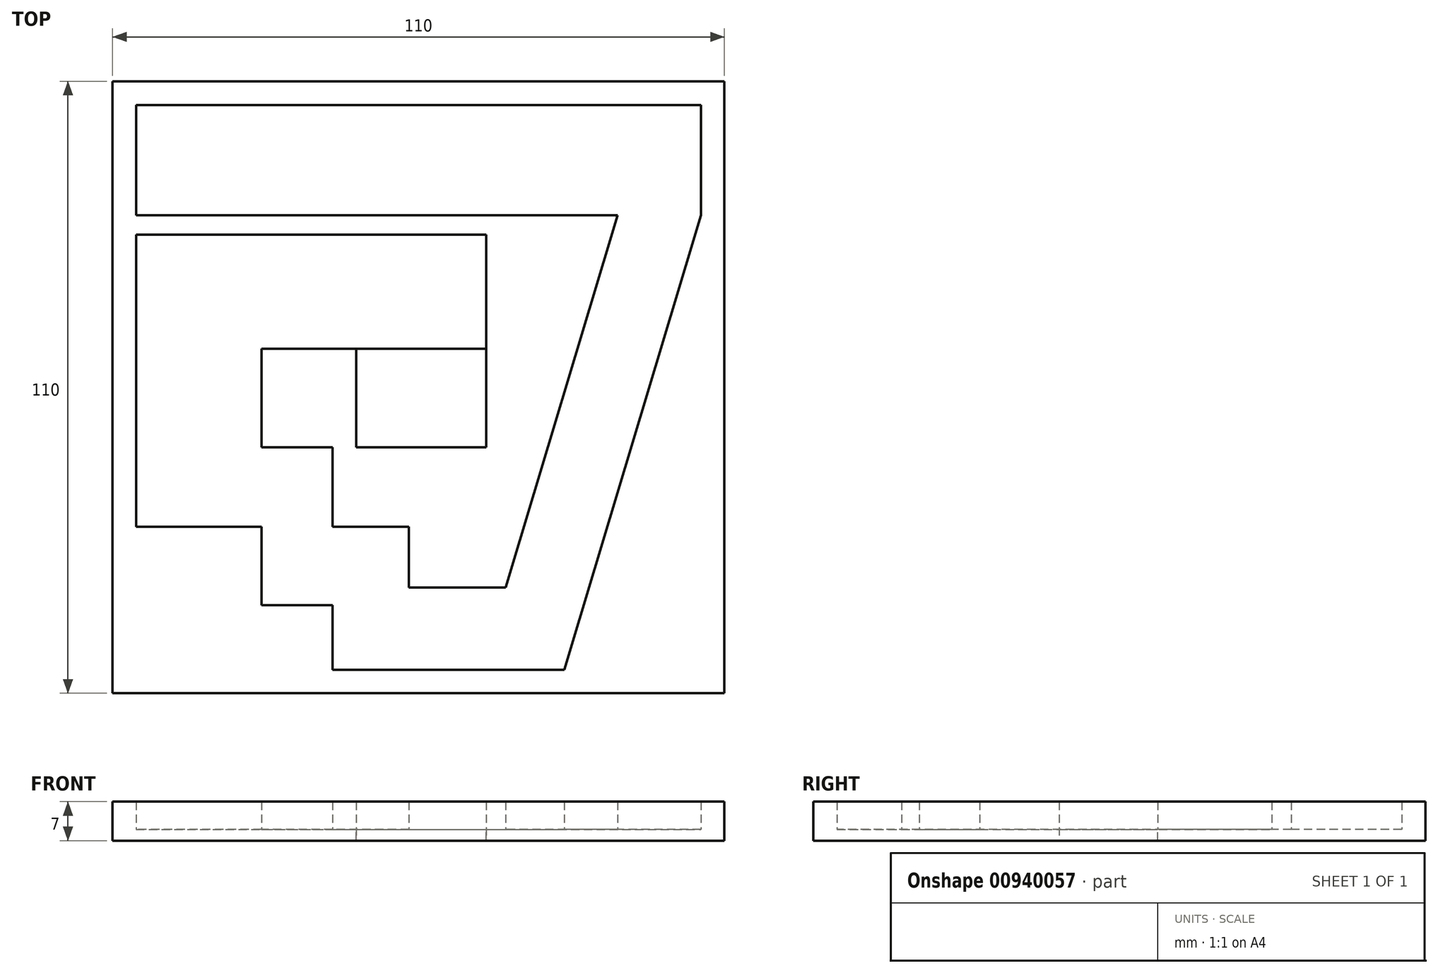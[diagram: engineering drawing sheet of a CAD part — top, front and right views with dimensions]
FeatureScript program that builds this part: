
annotation { "Feature Type Name" : "Feature", "Feature Type Description" : "" }
export const myFeature = defineFeature(function(context is Context, id is Id, definition is map)
    precondition{}
    {
        {
            var Q0;
            Q0=qCreatedBy(makeId("Top.planeOp"),FACE);
            var sketch = newSketch(context, id + "F0", { "sketchPlane" : qUnion([Q0])});
            skLineSegment(sketch, "E0.bottom", {"start": v(-49.05, 49.29) * mm, "end": v(52.5, 49.29) * mm});
            skLineSegment(sketch, "E0.top", {"start": v(-53.28, -56.48) * mm, "end": v(-13.73, -56.48) * mm});
            skLineSegment(sketch, "E0.right", {"start": v(52.5, 49.29) * mm, "end": v(52.5, 29.44) * mm});
            skLineSegment(sketch, "E1", {"start": v(-49.05, 29.44) * mm, "end": v(37.49, 29.44) * mm});
            skLineSegment(sketch, "E2", {"start": v(52.5, 29.44) * mm, "end": v(52.5, 29.44) * mm});
            skLineSegment(sketch, "E3", {"start": v(52.5, 29.44) * mm, "end": v(27.92, -52.25) * mm});
            skLineSegment(sketch, "E4", {"start": v(37.49, 29.44) * mm, "end": v(17.36, -37.48) * mm});
            skLineSegment(sketch, "E5", {"start": v(0, -37.48) * mm, "end": v(0, -26.57) * mm});
            skLineSegment(sketch, "E6", {"start": v(0, -26.57) * mm, "end": v(-13.73, -26.57) * mm});
            skLineSegment(sketch, "E7", {"start": v(-13.73, -26.57) * mm, "end": v(-13.73, -12.28) * mm});
            skLineSegment(sketch, "E8", {"start": v(-13.73, -12.28) * mm, "end": v(-26.47, -12.28) * mm});
            skLineSegment(sketch, "E9", {"start": v(-26.47, -12.28) * mm, "end": v(-26.47, 5.43) * mm});
            skLineSegment(sketch, "E10", {"start": v(-13.73, -52.25) * mm, "end": v(-13.73, -40.64) * mm});
            skLineSegment(sketch, "E11", {"start": v(-13.73, -40.64) * mm, "end": v(-26.47, -40.64) * mm});
            skLineSegment(sketch, "E12", {"start": v(-26.47, -40.64) * mm, "end": v(-26.47, -26.57) * mm});
            skLineSegment(sketch, "E13", {"start": v(-26.47, -26.57) * mm, "end": v(-49.05, -26.57) * mm});
            skLineSegment(sketch, "E14", {"start": v(-49.05, -26.57) * mm, "end": v(-49.05, 5.43) * mm});
            skLineSegment(sketch, "E15", {"start": v(-49.05, 5.43) * mm, "end": v(-49.05, 25.93) * mm});
            skLineSegment(sketch, "E16", {"start": v(-49.05, 25.93) * mm, "end": v(-26.47, 25.93) * mm});
            skLineSegment(sketch, "E17", {"start": v(-26.47, 25.93) * mm, "end": v(13.91, 25.93) * mm});
            skLineSegment(sketch, "E18", {"start": v(13.91, 25.93) * mm, "end": v(13.91, -12.28) * mm});
            skLineSegment(sketch, "E19", {"start": v(13.91, -12.28) * mm, "end": v(-9.5, -12.28) * mm});
            skLineSegment(sketch, "E20.top", {"start": v(-13.73, -52.25) * mm, "end": v(27.92, -52.25) * mm});
            skLineSegment(sketch, "E21.right", {"start": v(-9.5, 5.43) * mm, "end": v(-9.5, -12.28) * mm});
            skLineSegment(sketch, "E22.bottom", {"start": v(52.5, 49.29) * mm, "end": v(-49.05, 49.29) * mm});
            skLineSegment(sketch, "E22.top", {"start": v(56.72, 53.52) * mm, "end": v(-53.28, 53.52) * mm});
            skLineSegment(sketch, "E23", {"start": v(56.72, 53.52) * mm, "end": v(56.72, -56.48) * mm});
            skPoint(sketch, "E24.orphan", {"position": v(52.5, -56.48) * mm});
            skLineSegment(sketch, "E25", {"start": v(-13.73, -56.48) * mm, "end": v(56.72, -56.48) * mm});
            skLineSegment(sketch, "E26.bottom", {"start": v(-9.5, 5.43) * mm, "end": v(13.91, 5.43) * mm});
            skLineSegment(sketch, "E26.top", {"start": v(-9.5, -12.28) * mm, "end": v(13.91, -12.28) * mm});
            skLineSegment(sketch, "E26.right", {"start": v(13.91, 5.43) * mm, "end": v(13.91, -12.28) * mm});
            skLineSegment(sketch, "E27.right", {"start": v(-49.05, 49.29) * mm, "end": v(-49.05, 29.44) * mm});
            skPoint(sketch, "E0.left.start.orphan", {"position": v(-53.28, 49.29) * mm});
            skLineSegment(sketch, "E28", {"start": v(-53.28, 53.52) * mm, "end": v(-53.28, -56.48) * mm});
            skPoint(sketch, "E29.start.orphan", {"position": v(-13.73, 5.43) * mm});
            skLineSegment(sketch, "E30", {"start": v(-26.47, 5.43) * mm, "end": v(-9.5, 5.43) * mm});
            skLineSegment(sketch, "E31", {"start": v(0, -37.48) * mm, "end": v(17.36, -37.48) * mm});
            skPoint(sketch, "E32.orphan", {"position": v(0, -40.64) * mm});
            skSolve(sketch);
        }
        {
            var Q0;
            Q0=makeQuery(id+"F0.imprint","IMPRINT",FACE,{"disambiguationData":[TD([[makeQuery(id+"F0.imprint","IMPRINT",EDGE,{"derivedFrom":sQuery(id+"F0.wireOp",EDGE,"E8")}),-1.0]])]});
            var Q1;
            {var subQ4=sQuery(id+"F0.wireOp",EDGE,"E1");Q1=makeQuery(id+"F0.imprint","IMPRINT",FACE,{"disambiguationData":[TD([[makeQuery(id+"F0.imprint","IMPRINT",EDGE,{"derivedFrom":subQ4}),-1.0]])]});}
            var Q2;
            {var subQ4=sQuery(id+"F0.wireOp",EDGE,"E0.right");var subQ6=sQuery(id+"F0.wireOp",EDGE,"E0.top");var subQ8=makeQuery(id+"F0.imprint","INTERSECT",VERTEX,{"derivedFrom":[subQ6,subQ4]});Q2=makeQuery(id+"F0.imprint","IMPRINT",FACE,{"disambiguationData":[TD([[makeQuery(id+"F0.imprint","IMPRINT",EDGE,{"disambiguationData":[TD([[subQ8,1.0]])],"derivedFrom":subQ6}),1.0]])]});}
            var Q3;
            {var subQ3=sQuery(id+"F0.wireOp",EDGE,"E20.top");Q3=makeQuery(id+"F0.imprint","IMPRINT",FACE,{"disambiguationData":[TD([[makeQuery(id+"F0.imprint","IMPRINT",EDGE,{"derivedFrom":subQ3}),-1.0]])]});}
            extrude(context, id + "F1", {"entities" : qUnion([Q0, Q1, Q2, Q3]), "depth" : 5 * mm, "offsetDistance" : 25 * mm});
        }
        {
            var Q0;
            {var subQ0=sQuery(id+"F0.wireOp",EDGE,"E1");Q0=makeQuery(id+"F0.imprint","IMPRINT",FACE,{"disambiguationData":[TD([[makeQuery(id+"F0.imprint","IMPRINT",EDGE,{"derivedFrom":subQ0}),1.0]])]});}
            var Q1;
            Q1=makeQuery(id+"F0.imprint","IMPRINT",FACE,{"disambiguationData":[TD([[makeQuery(id+"F0.imprint","IMPRINT",EDGE,{"derivedFrom":sQuery(id+"F0.wireOp",EDGE,"E3")}),1.0]])]});
            var Q2;
            {var subQ0=sQuery(id+"F0.wireOp",EDGE,"E0.top");Q2=makeQuery(id+"F0.imprint","IMPRINT",FACE,{"disambiguationData":[TD([[makeQuery(id+"F0.imprint","IMPRINT",EDGE,{"derivedFrom":subQ0}),1.0]])]});}
            var Q3;
            Q3=makeQuery(id+"F0.imprint","IMPRINT",FACE,{"disambiguationData":[TD([[makeQuery(id+"F0.imprint","IMPRINT",EDGE,{"derivedFrom":sQuery(id+"F0.wireOp",EDGE,"E8")}),-1.0]])]});
            extrude(context, id + "F2", {"entities" : qUnion([Q0, Q1, Q2, Q3]), "operationType" : NewBodyOperationType.ADD, "oppositeDirection" : true, "depth" : 2 * mm, "offsetDistance" : 25 * mm});
        }
    });
